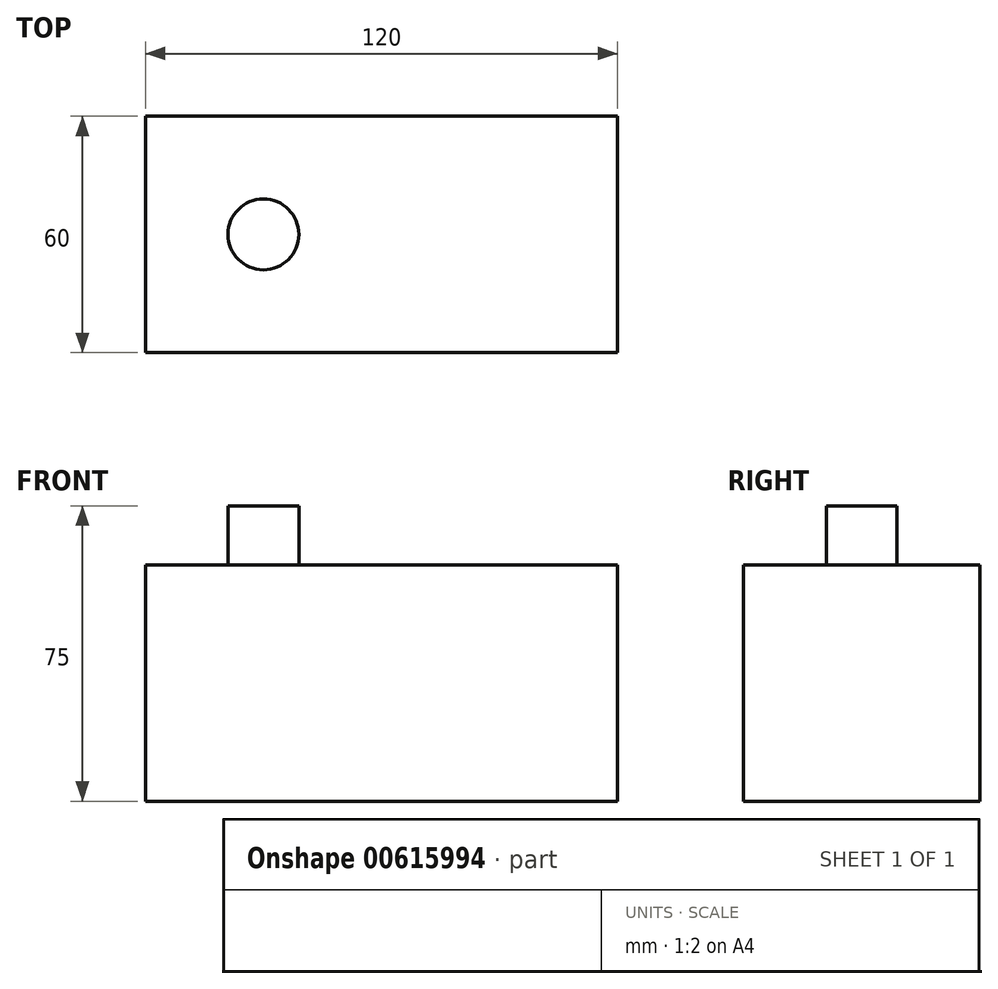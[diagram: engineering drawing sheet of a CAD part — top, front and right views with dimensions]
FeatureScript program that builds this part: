
annotation { "Feature Type Name" : "Feature", "Feature Type Description" : "" }
export const myFeature = defineFeature(function(context is Context, id is Id, definition is map)
    precondition{}
    {
        {
            var Q0;
            Q0=qCreatedBy(makeId("Front.planeOp"),FACE);
            var sketch = newSketch(context, id + "F0", { "sketchPlane" : qUnion([Q0])});
            skLineSegment(sketch, "E0.bottom", {"start": v(0, 0) * mm, "end": v(120, 0) * mm});
            skLineSegment(sketch, "E0.top", {"start": v(0, 60) * mm, "end": v(120, 60) * mm});
            skLineSegment(sketch, "E0.left", {"start": v(0, 0) * mm, "end": v(0, 60) * mm});
            skLineSegment(sketch, "E0.right", {"start": v(120, 0) * mm, "end": v(120, 60) * mm});
            skSolve(sketch);
        }
        {
            var Q0;
            Q0 = qSketchRegion(id + "F0", true);
            extrude(context, id + "F1", {"entities" : qUnion([Q0]), "endBound" : BoundingType.SYMMETRIC, "depth" : 60 * mm, "offsetDistance" : 25 * mm});
        }
        {
            var Q0;
            Q0=makeQuery(id+"F1.opExtrude","SWEPT_FACE",FACE,{"disambiguationData":[OSD([sQuery(id+"F0.wireOp",EDGE,"E0.top")])]});
            var sketch = newSketch(context, id + "F2", { "sketchPlane" : qUnion([Q0])});
            skLineSegment(sketch, "E1", {"start": v(30, 30) * mm, "end": v(30, -30) * mm, "construction": true});
            skLineSegment(sketch, "E2", {"start": v(60, 30) * mm, "end": v(60, -30) * mm, "construction": true});
            skLineSegment(sketch, "E3", {"start": v(0, 0) * mm, "end": v(120, 0) * mm, "construction": true});
            skLineSegment(sketch, "E4", {"start": v(90, 30) * mm, "end": v(90, -30) * mm, "construction": true});
            skCircle(sketch, "E5", {"center": v(30, 0) * mm, "radius": 9 * mm});
            skCircle(sketch, "E6", {"center": v(60, 0) * mm, "radius": 9 * mm});
            skCircle(sketch, "E7", {"center": v(90, 0) * mm, "radius": 9 * mm});
            skSolve(sketch);
        }
        {
            var Q0;
            Q0=makeQuery(id+"F2.imprint","IMPRINT",FACE,{"disambiguationData":[TD([[makeQuery(id+"F2.imprint","IMPRINT",EDGE,{"derivedFrom":sQuery(id+"F2.wireOp",EDGE,"E5")}),1.0]])]});
            extrude(context, id + "F3", {"entities" : qUnion([Q0]), "operationType" : NewBodyOperationType.ADD, "depth" : 15 * mm, "offsetDistance" : 25 * mm});
        }
        {
            var Q0;
            Q0 = qSketchRegion(id + "F2", true);
            extrude(context, id + "F4", {"entities" : qUnion([Q0]), "operationType" : NewBodyOperationType.ADD, "depth" : -15 * mm, "offsetDistance" : 25 * mm});
        }
        {
            var Q0;
            Q0=sQuery(id+"F2.wireOp",EDGE,"E6");
            extrude(context, id + "F5", {"bodyType" : ToolBodyType.SURFACE, "surfaceEntities" : qUnion([Q0]), "depth" : -15 * mm, "offsetDistance" : 25 * mm});
        }
        {
            var Q0;
            Q0 = qSketchRegion(id + "F0", true);
            extrude(context, id + "F6", {"entities" : qUnion([Q0]), "operationType" : NewBodyOperationType.ADD, "depth" : 25 * mm, "offsetDistance" : 25 * mm});
        }
    });
